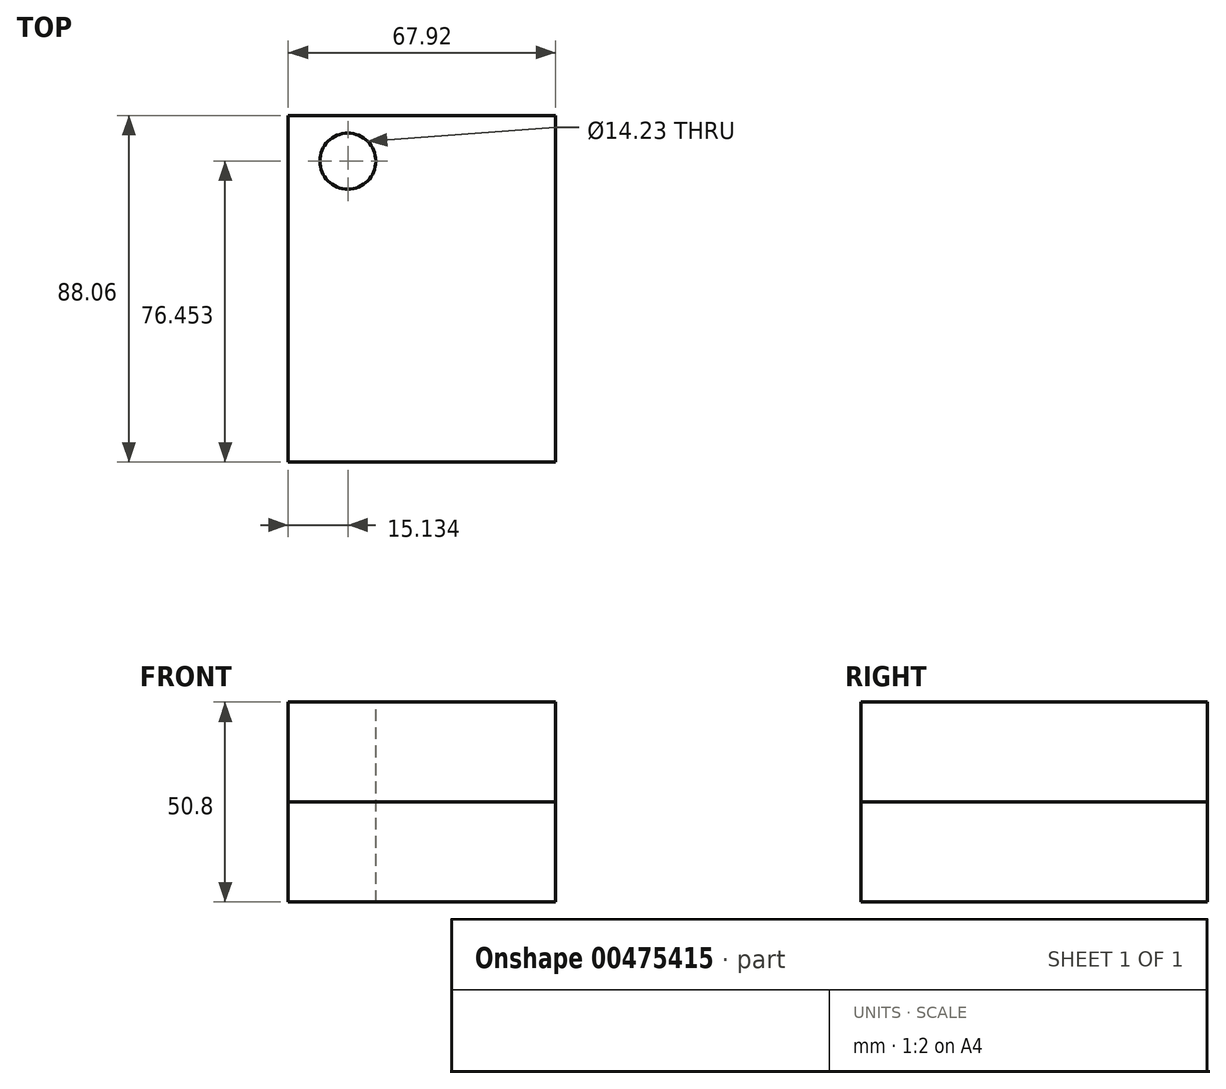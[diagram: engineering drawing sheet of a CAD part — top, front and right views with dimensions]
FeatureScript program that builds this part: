
annotation { "Feature Type Name" : "Feature", "Feature Type Description" : "" }
export const myFeature = defineFeature(function(context is Context, id is Id, definition is map)
    precondition{}
    {
        {
            var Q0;
            Q0=qCreatedBy(makeId("Top.planeOp"),FACE);
            var sketch = newSketch(context, id + "F0", { "sketchPlane" : qUnion([Q0])});
            skLineSegment(sketch, "E0.bottom", {"start": v(33.96, 44.03) * mm, "end": v(-33.96, 44.03) * mm});
            skLineSegment(sketch, "E0.top", {"start": v(33.96, -44.03) * mm, "end": v(-33.96, -44.03) * mm});
            skLineSegment(sketch, "E0.left", {"start": v(33.96, 44.03) * mm, "end": v(33.96, -44.03) * mm});
            skLineSegment(sketch, "E0.right", {"start": v(-33.96, 44.03) * mm, "end": v(-33.96, -44.03) * mm});
            skPoint(sketch, "E0.middle", {"position": v(0, 0) * mm});
            skSolve(sketch);
        }
        {
            var Q0;
            Q0=makeQuery(id+"F0.imprint","IMPRINT",FACE,{"disambiguationData":[TD([[makeQuery(id+"F0.imprint","IMPRINT",EDGE,{"derivedFrom":sQuery(id+"F0.wireOp",EDGE,"E0.bottom")}),1.0]])]});
            extrude(context, id + "F1", {"entities" : qUnion([Q0]), "endBound" : BoundingType.SYMMETRIC, "depth" : 50.8 * mm});
        }
        {
            var Q0;
            Q0=makeQuery(id+"F1.opExtrude","CAP_FACE",FACE,{"disambiguationData":[OSD([sQuery(id+"F0.wireOp",EDGE,"E0.bottom"),sQuery(id+"F0.wireOp",EDGE,"E0.top"),sQuery(id+"F0.wireOp",EDGE,"E0.left"),sQuery(id+"F0.wireOp",EDGE,"E0.right")])],"isStart":false});
            var sketch = newSketch(context, id + "F2", { "sketchPlane" : qUnion([Q0])});
            skCircle(sketch, "E1", {"center": v(-18.83, 32.42) * mm, "radius": 7.11 * mm});
            skSolve(sketch);
        }
        {
            var Q0;
            Q0=makeQuery(id+"F2.imprint","IMPRINT",FACE,{"disambiguationData":[TD([[makeQuery(id+"F2.imprint","IMPRINT",EDGE,{"derivedFrom":sQuery(id+"F2.wireOp",EDGE,"E1")}),1.0]])]});
            var Q1;
            Q1=sQuery(id+"F2.wireOp",EDGE,"E1");
            extrude(context, id + "F3", {"entities" : qUnion([Q0]), "operationType" : NewBodyOperationType.REMOVE, "surfaceEntities" : qUnion([Q1]), "endBound" : BoundingType.THROUGH_ALL, "oppositeDirection" : true, "depth" : 25.4 * mm});
        }
        {
            var Q0;
            Q0=makeQuery(id+"F0.imprint","IMPRINT",FACE,{"disambiguationData":[TD([[makeQuery(id+"F0.imprint","IMPRINT",EDGE,{"derivedFrom":sQuery(id+"F0.wireOp",EDGE,"E0.bottom")}),1.0]])]});
            extrude(context, id + "F4", {"entities" : qUnion([Q0]), "depth" : 25.4 * mm});
        }
    });
